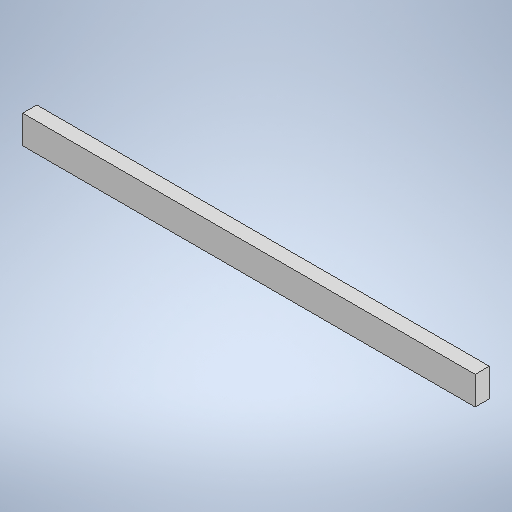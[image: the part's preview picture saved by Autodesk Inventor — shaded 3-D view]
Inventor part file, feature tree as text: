
AUTODESK INVENTOR PART (.ipt)
format: ipt  version: 2025 (Build 290162000, 162)  size: 239,616 bytes
history: native  units: in
note: dims shown in document units (in); Inventor stores cm internally (conversion verified against a paired STEP export)
features: extrude x1, sketch x1
ambient origin geometry x8: Origin, YZ Plane, XZ Plane, XY Plane, X Axis, Y Axis, Z Axis, Center Point
bodies: Solid1 (feature_tree)
feature tree (2):
  extrude  "Extrusion1"  Depth=0.7874in TaperAngle=0.0deg
  sketch  "Sketch1"  dims[d0=25.1969in d1=0.7874in d2=0.0in d3=1.5748in]
